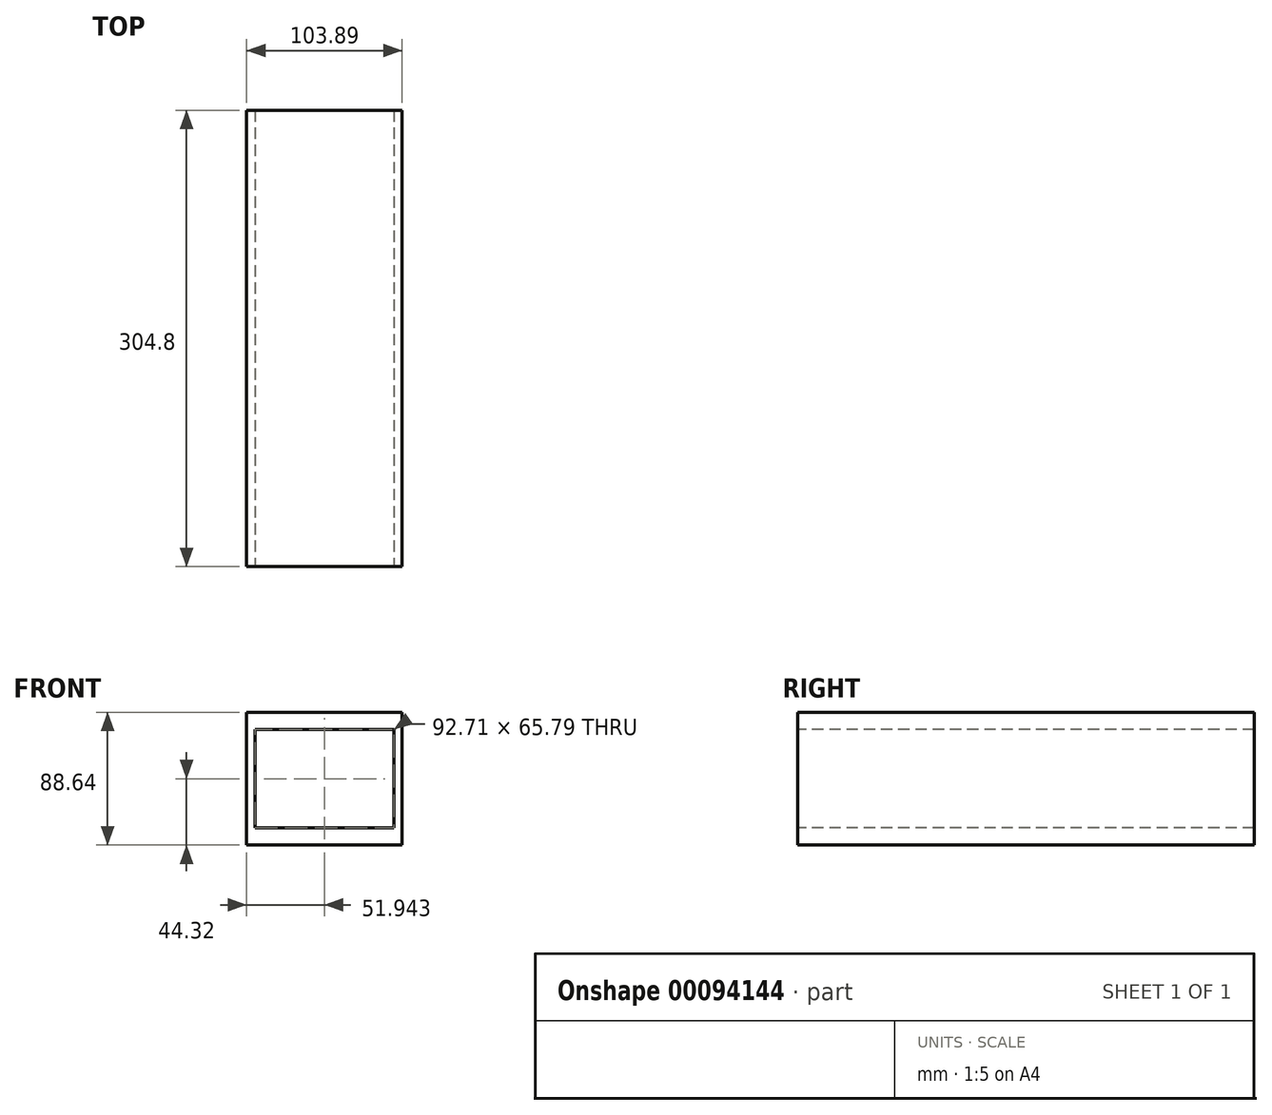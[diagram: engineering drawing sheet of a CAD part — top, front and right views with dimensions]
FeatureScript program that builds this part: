
annotation { "Feature Type Name" : "Feature", "Feature Type Description" : "" }
export const myFeature = defineFeature(function(context is Context, id is Id, definition is map)
    precondition{}
    {
        {
            var Q0;
            Q0=qCreatedBy(makeId("Right.planeOp"),FACE);
            var sketch = newSketch(context, id + "F0", { "sketchPlane" : qUnion([Q0])});
            skLineSegment(sketch, "E0.bottom", {"start": v(-152.4, -44.32) * mm, "end": v(152.4, -44.32) * mm});
            skLineSegment(sketch, "E0.top", {"start": v(-152.4, 44.32) * mm, "end": v(152.4, 44.32) * mm});
            skLineSegment(sketch, "E0.left", {"start": v(-152.4, -44.32) * mm, "end": v(-152.4, 44.32) * mm});
            skLineSegment(sketch, "E0.right", {"start": v(152.4, -44.32) * mm, "end": v(152.4, 44.32) * mm});
            skPoint(sketch, "E0.middle", {"position": v(0, 0) * mm});
            skSolve(sketch);
        }
        {
            var Q0;
            Q0=makeQuery(id+"F0.imprint","IMPRINT",FACE,{"disambiguationData":[TD([[makeQuery(id+"F0.imprint","IMPRINT",EDGE,{"derivedFrom":sQuery(id+"F0.wireOp",EDGE,"E0.bottom")}),1.0]])]});
            extrude(context, id + "F1", {"entities" : qUnion([Q0]), "depth" : 103.89 * mm});
        }
        {
            var Q0;
            Q0=makeQuery(id+"F1.opExtrude","SWEPT_FACE",FACE,{"disambiguationData":[OSD([sQuery(id+"F0.wireOp",EDGE,"E0.left")])]});
            var sketch = newSketch(context, id + "F2", { "sketchPlane" : qUnion([Q0])});
            skSolve(sketch);
        }
        {
            var Q0;
            {var subQ0=sQuery(id+"F0.wireOp",EDGE,"E0.left");Q0=makeQuery(id+"F2.imprint","IMPRINT",FACE,{"disambiguationData":[TD([[makeQuery(id+"F2.imprint","IMPRINT",EDGE,{"derivedFrom":makeQuery(id+"F1.opExtrude","CAP_EDGE",EDGE,{"disambiguationData":[OSD([subQ0])],"isStart":true})}),-1.0]])]});}
            var sketch = newSketch(context, id + "F3", { "sketchPlane" : qUnion([Q0])});
            skLineSegment(sketch, "E1.bottom", {"start": v(5.59, -32.9) * mm, "end": v(98.3, -32.9) * mm});
            skLineSegment(sketch, "E1.top", {"start": v(5.59, 32.9) * mm, "end": v(98.3, 32.9) * mm});
            skLineSegment(sketch, "E1.left", {"start": v(5.59, -32.9) * mm, "end": v(5.59, 32.9) * mm});
            skLineSegment(sketch, "E1.right", {"start": v(98.3, -32.9) * mm, "end": v(98.3, 32.9) * mm});
            skPoint(sketch, "E1.middle", {"position": v(51.94, 0) * mm});
            skSolve(sketch);
        }
        {
            var Q0;
            Q0 = qSketchRegion(id + "F3", true);
            extrude(context, id + "F4", {"entities" : qUnion([Q0]), "operationType" : NewBodyOperationType.REMOVE, "oppositeDirection" : true, "depth" : 1270 * mm});
        }
    });
